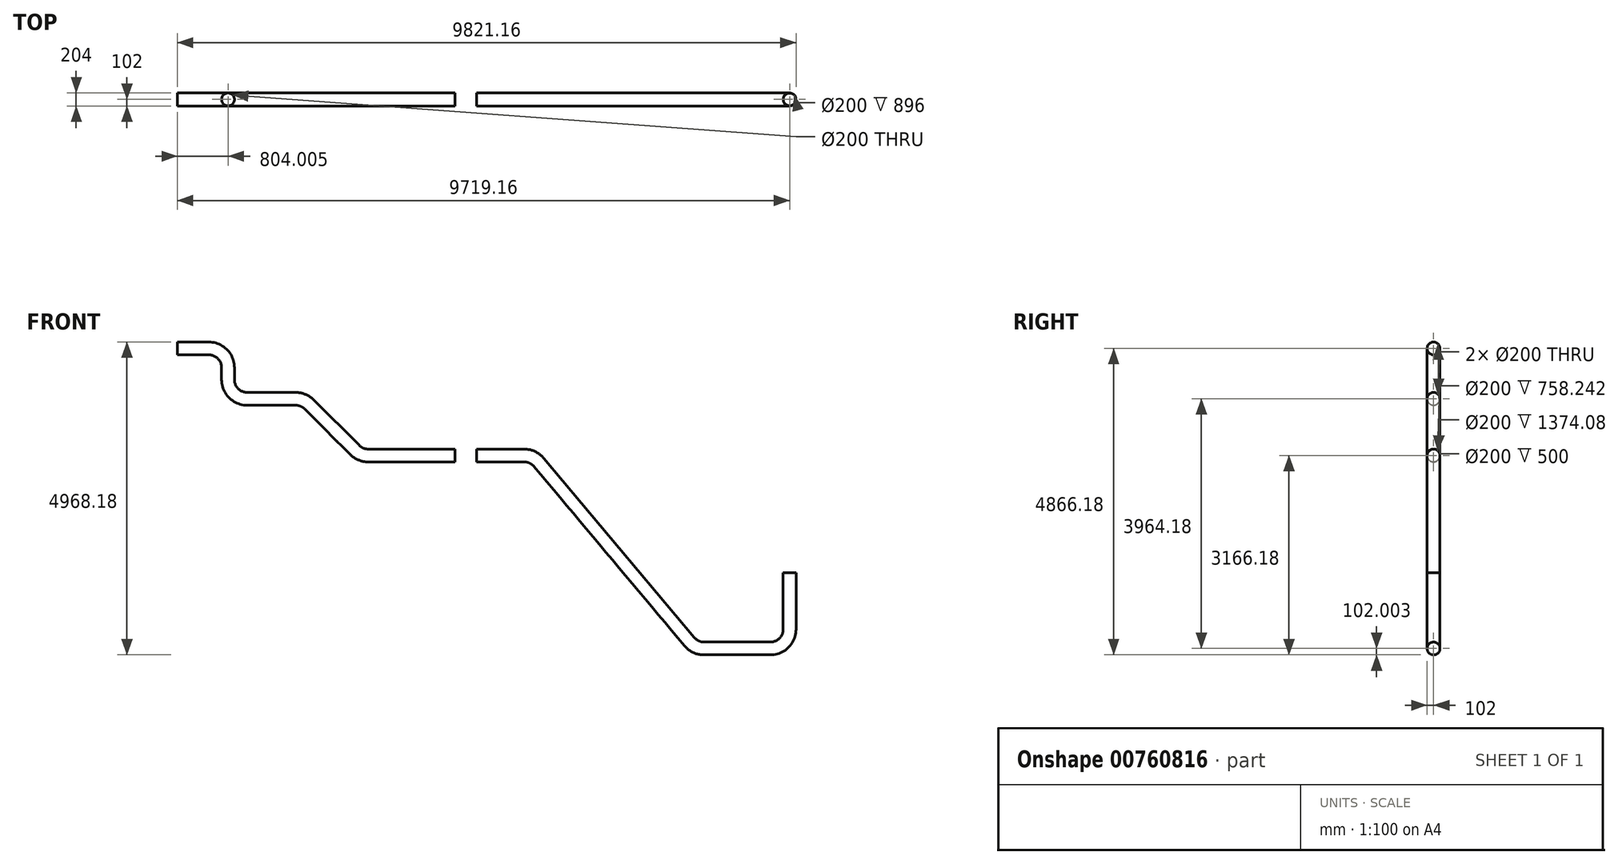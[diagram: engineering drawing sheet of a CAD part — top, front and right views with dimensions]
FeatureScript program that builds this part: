
annotation { "Feature Type Name" : "Feature", "Feature Type Description" : "" }
export const myFeature = defineFeature(function(context is Context, id is Id, definition is map)
    precondition{}
    {
        {
            var Q0;
            Q0=qCreatedBy(makeId("Front.planeOp"),FACE);
            var sketch = newSketch(context, id + "F0", { "sketchPlane" : qUnion([Q0])});
            skLineSegment(sketch, "E0", {"start": v(1020.48, -434.89) * mm, "end": v(1778.73, -434.89) * mm});
            skLineSegment(sketch, "E1", {"start": v(2011.6, -543.48) * mm, "end": v(4400.52, -3390.47) * mm});
            skLineSegment(sketch, "E2", {"start": v(4633.4, -3499.07) * mm, "end": v(5687.64, -3499.07) * mm});
            skLineSegment(sketch, "E3", {"start": v(5991.64, -3195.07) * mm, "end": v(5991.64, -2299.07) * mm});
            skPoint(sketch, "E4.visualSharp", {"position": v(1920.48, -434.89) * mm});
            skArc(sketch, "E4.filletArc", {"start": v(2011.6, -543.48) * mm, "mid": v(1907.2, -463.37) * mm, "end": v(1778.73, -434.89) * mm});
            skPoint(sketch, "E5.visualSharp", {"position": v(4491.64, -3499.07) * mm});
            skArc(sketch, "E5.filletArc", {"start": v(4400.52, -3390.47) * mm, "mid": v(4504.92, -3470.58) * mm, "end": v(4633.4, -3499.07) * mm});
            skPoint(sketch, "E6.visualSharp", {"position": v(5991.64, -3499.07) * mm});
            skArc(sketch, "E6.filletArc", {"start": v(5687.64, -3499.07) * mm, "mid": v(5902.6, -3410.03) * mm, "end": v(5991.64, -3195.07) * mm});
            skLineSegment(sketch, "E7", {"start": v(1020.48, -434.89) * mm, "end": v(1020.48, -359.89) * mm});
            skLineSegment(sketch, "E8", {"start": v(676.48, -359.89) * mm, "end": v(676.48, -434.89) * mm});
            skLineSegment(sketch, "E9", {"start": v(676.48, -434.89) * mm, "end": v(-697.6, -434.89) * mm});
            skLineSegment(sketch, "E10", {"start": v(-912.55, -345.85) * mm, "end": v(-1634.48, 376.07) * mm});
            skLineSegment(sketch, "E11", {"start": v(-1849.44, 465.11) * mm, "end": v(-2619.52, 465.11) * mm});
            skLineSegment(sketch, "E12", {"start": v(-2923.52, 769.11) * mm, "end": v(-2923.52, 961.11) * mm});
            skLineSegment(sketch, "E13", {"start": v(-3227.52, 1265.11) * mm, "end": v(-3727.52, 1265.11) * mm});
            skPoint(sketch, "E14.visualSharp", {"position": v(-2923.52, 465.11) * mm});
            skArc(sketch, "E14.filletArc", {"start": v(-2923.52, 769.11) * mm, "mid": v(-2834.48, 554.15) * mm, "end": v(-2619.52, 465.11) * mm});
            skPoint(sketch, "E15.visualSharp", {"position": v(-2923.52, 1265.11) * mm});
            skArc(sketch, "E15.filletArc", {"start": v(-2923.52, 961.11) * mm, "mid": v(-3012.55, 1176.07) * mm, "end": v(-3227.52, 1265.11) * mm});
            skPoint(sketch, "E16.visualSharp", {"position": v(-1723.52, 465.11) * mm});
            skArc(sketch, "E16.filletArc", {"start": v(-1634.48, 376.07) * mm, "mid": v(-1733.1, 441.97) * mm, "end": v(-1849.44, 465.11) * mm});
            skPoint(sketch, "E17.visualSharp", {"position": v(-823.52, -434.89) * mm});
            skArc(sketch, "E17.filletArc", {"start": v(-912.55, -345.85) * mm, "mid": v(-813.93, -411.75) * mm, "end": v(-697.6, -434.89) * mm});
            skLineSegment(sketch, "E18", {"start": v(-3727.52, 1205.17) * mm, "end": v(-3727.52, 1265.11) * mm});
            skLineSegment(sketch, "E19", {"start": v(5991.64, -2299.07) * mm, "end": v(6181.16, -2299.07) * mm});
            skSolve(sketch);
        }
        {
            var Q0;
            Q0=sQuery(id+"F0.wireOp",EDGE,"E13");
            var Q1;
            Q1=sQuery(id+"F0.wireOp",EDGE,"E15.filletArc");
            var Q2;
            Q2=sQuery(id+"F0.wireOp",EDGE,"E12");
            var Q3;
            Q3=sQuery(id+"F0.wireOp",EDGE,"E14.filletArc");
            var Q4;
            Q4=sQuery(id+"F0.wireOp",EDGE,"E11");
            var Q5;
            Q5=sQuery(id+"F0.wireOp",EDGE,"E16.filletArc");
            var Q6;
            Q6=sQuery(id+"F0.wireOp",EDGE,"E10");
            var Q7;
            Q7=sQuery(id+"F0.wireOp",EDGE,"E17.filletArc");
            var Q8;
            Q8=sQuery(id+"F0.wireOp",EDGE,"E9");
            var Q9;
            Q9=sQuery(id+"F0.wireOp",EDGE,"E0");
            var Q10;
            Q10=sQuery(id+"F0.wireOp",EDGE,"E4.filletArc");
            var Q11;
            Q11=sQuery(id+"F0.wireOp",EDGE,"E1");
            var Q12;
            Q12=sQuery(id+"F0.wireOp",EDGE,"E5.filletArc");
            var Q13;
            Q13=sQuery(id+"F0.wireOp",EDGE,"E2");
            var Q14;
            Q14=sQuery(id+"F0.wireOp",EDGE,"E6.filletArc");
            var Q15;
            Q15=sQuery(id+"F0.wireOp",EDGE,"E3");
            extrude(context, id + "F1", {"bodyType" : ToolBodyType.SURFACE, "surfaceEntities" : qUnion([Q0, Q1, Q2, Q3, Q4, Q5, Q6, Q7, Q8, Q9, Q10, Q11, Q12, Q13, Q14, Q15]), "depth" : 25 * mm, "offsetDistance" : 25.4 * mm});
        }
        {
            var Q0;
            Q0=sQuery(id+"F0.wireOp",EDGE,"E18");
            var Q1;
            Q1=sQuery(id+"F0.wireOp",EDGE,"E8");
            var Q2;
            Q2=sQuery(id+"F0.wireOp",EDGE,"E7");
            var Q3;
            Q3=sQuery(id+"F0.wireOp",EDGE,"E19");
            extrude(context, id + "F2", {"bodyType" : ToolBodyType.SURFACE, "surfaceEntities" : qUnion([Q0, Q1, Q2, Q3]), "depth" : 25 * mm, "offsetDistance" : 25.4 * mm});
        }
        {
            var Q0;
            Q0=makeQuery(id+"F2.opExtrude","SWEPT_FACE",FACE,{"disambiguationData":[OSD([sQuery(id+"F0.wireOp",EDGE,"E18")])]});
            var sketch = newSketch(context, id + "F3", { "sketchPlane" : qUnion([Q0])});
            skPoint(sketch, "E20.0", {"position": v(0, 1265.11) * mm});
            skCircle(sketch, "E21", {"center": v(0, 1265.11) * mm, "radius": 102 * mm});
            skCircle(sketch, "E22.0", {"center": v(0, 1265.11) * mm, "radius": 100 * mm});
            skSolve(sketch);
        }
        {
            var Q0;
            Q0=makeQuery(id+"F3.imprint","IMPRINT",FACE,{"disambiguationData":[TD([[makeQuery(id+"F3.imprint","IMPRINT",EDGE,{"derivedFrom":sQuery(id+"F3.wireOp",EDGE,"E21")}),1.0]])]});
            var Q1;
            Q1=sQuery(id+"F0.wireOp",EDGE,"E13");
            var Q2;
            Q2=sQuery(id+"F0.wireOp",EDGE,"E15.filletArc");
            var Q3;
            Q3=sQuery(id+"F0.wireOp",EDGE,"E12");
            var Q4;
            Q4=sQuery(id+"F0.wireOp",EDGE,"E14.filletArc");
            var Q5;
            Q5=sQuery(id+"F0.wireOp",EDGE,"E11");
            var Q6;
            Q6=sQuery(id+"F0.wireOp",EDGE,"E16.filletArc");
            var Q7;
            Q7=sQuery(id+"F0.wireOp",EDGE,"E10");
            var Q8;
            Q8=sQuery(id+"F0.wireOp",EDGE,"E17.filletArc");
            var Q9;
            Q9=sQuery(id+"F0.wireOp",EDGE,"E9");
            sweep(context, id + "F4", {"profiles" : qUnion([Q0]), "path" : qUnion([Q1, Q2, Q3, Q4, Q5, Q6, Q7, Q8, Q9])});
        }
        {
            var Q0;
            Q0=makeQuery(id+"F2.opExtrude","SWEPT_FACE",FACE,{"disambiguationData":[OSD([sQuery(id+"F0.wireOp",EDGE,"E7")])]});
            var sketch = newSketch(context, id + "F5", { "sketchPlane" : qUnion([Q0])});
            skCircle(sketch, "E23", {"center": v(0, -434.89) * mm, "radius": 102 * mm});
            skCircle(sketch, "E24.0", {"center": v(0, -434.89) * mm, "radius": 100 * mm});
            skSolve(sketch);
        }
        {
            var Q0;
            {var subQ0=sQuery(id+"F5.wireOp",EDGE,"E23");var subQ1=sQuery(id+"F0.wireOp",EDGE,"E7");var subQ2=makeQuery(id+"F2.opExtrude","CAP_EDGE",EDGE,{"disambiguationData":[OSD([subQ1])],"isStart":true});var subQ3=makeQuery(id+"F5.imprint","INTERSECT",VERTEX,{"derivedFrom":[subQ2,subQ0]});Q0=makeQuery(id+"F5.imprint","IMPRINT",FACE,{"disambiguationData":[TD([[makeQuery(id+"F5.imprint","IMPRINT",EDGE,{"disambiguationData":[TD([[subQ3,1.0]])],"derivedFrom":subQ0}),1.0]])]});}
            var Q1;
            Q1=sQuery(id+"F0.wireOp",EDGE,"E0");
            var Q2;
            Q2=sQuery(id+"F0.wireOp",EDGE,"E4.filletArc");
            var Q3;
            Q3=sQuery(id+"F0.wireOp",EDGE,"E1");
            var Q4;
            Q4=sQuery(id+"F0.wireOp",EDGE,"E5.filletArc");
            var Q5;
            Q5=sQuery(id+"F0.wireOp",EDGE,"E2");
            var Q6;
            Q6=sQuery(id+"F0.wireOp",EDGE,"E6.filletArc");
            var Q7;
            Q7=sQuery(id+"F0.wireOp",EDGE,"E3");
            sweep(context, id + "F6", {"profiles" : qUnion([Q0]), "path" : qUnion([Q1, Q2, Q3, Q4, Q5, Q6, Q7])});
        }
    });
